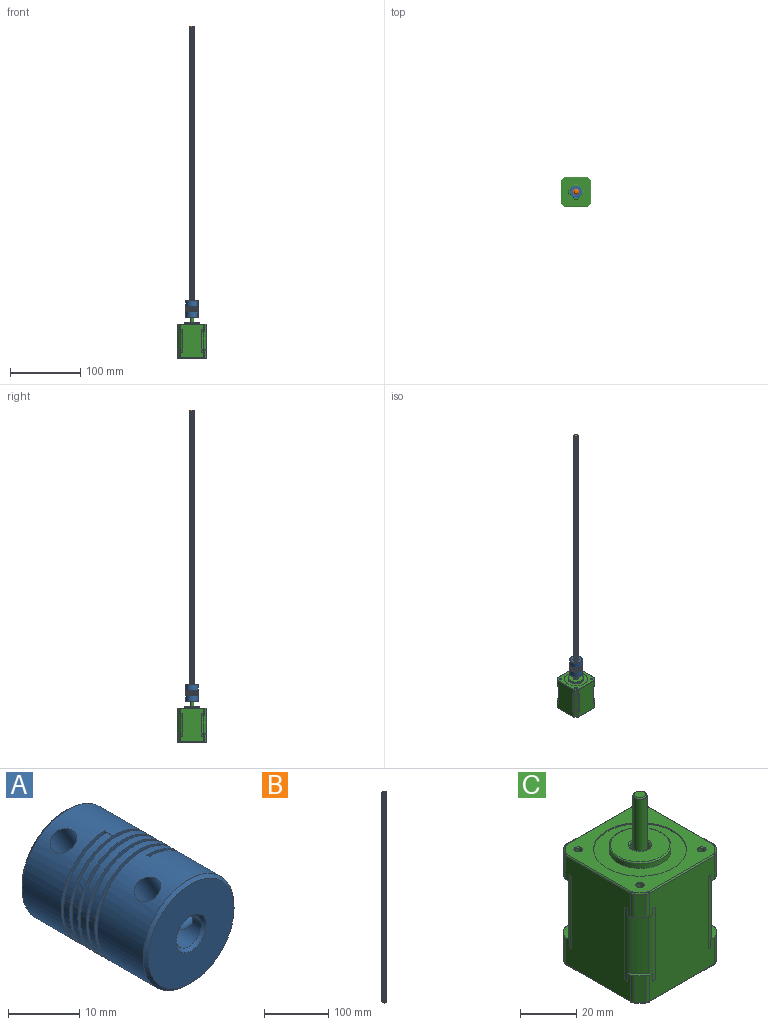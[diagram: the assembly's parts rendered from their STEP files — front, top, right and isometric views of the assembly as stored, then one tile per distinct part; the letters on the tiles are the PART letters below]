
ASSEMBLY  parts=3 mates=2
PART A: 27 faces, bbox 18.3x25x18.3 mm
  f0: cone r=2.75mm half-angle=45deg, axis (0,-1,0), area 12.2mm2, adj f1,f9
  f1: plane 17.31x17mm, normal (0,-1,0), area 198.7mm2, adj f0,f12
  f2: cylinder r=4mm len=4mm, axis (0,-1,0), area 1.3mm2, adj f5,f6,f18
  f3: cylinder r=4mm len=9.42mm, axis (0,-1,0), area 185mm2, adj f4,f10,f14,f16,f17,f18,f19
  f4: cylinder r=4mm len=8mm, axis (0,-1,0), area 29.3mm2, adj f3,f5,f18,f19
  f5: cylinder r=4mm len=8mm, axis (0,-1,0), area 25.1mm2, adj f2,f4,f6,f18,f19
  f6: plane 8.06x7.8mm, normal (0,1,0), area 21.4mm2, adj f2,f5,f7,f18,f19
  f7: cylinder r=2.5mm len=5mm, axis (0,1,0), area 8.3mm2, adj f6,f8,f18,f19
  f8: cylinder r=2.5mm len=5mm, axis (0,1,0), area 18.3mm2, adj f7,f9,f18,f19
  f9: cylinder r=2.5mm len=10.16mm, axis (0,1,0), area 118.5mm2, adj f0,f8,f11,f13,f15,f18,f19
  f10: cone r=4.25mm half-angle=45deg, axis (0,1,0), area 18.9mm2, adj f3,f20
  f11: plane 6.5x0.5mm, normal (1,0,0), area 3.3mm2, adj f9,f18,f19,f25
  f12: cone r=8.75mm half-angle=45deg, axis (0,1,0), area 38.9mm2, adj f1,f25
  f13: cylinder r=2mm len=8.5mm, axis (-0.5,0,0.87), area 86.6mm2, adj f9,f25
  f14: cylinder r=2mm len=6.79mm, axis (-0.5,0,0.87), area 64.8mm2, adj f3,f24
  f15: cylinder r=2mm len=7.5mm, axis (1,0,0), area 86.6mm2, adj f9,f25
  f16: cylinder r=2mm len=5.54mm, axis (1,0,0), area 64.8mm2, adj f3,f24
  f17: plane 5x0.5mm, normal (-1,0,0), area 2.5mm2, adj f3,f18,f19,f24
  f18: bspline ~18.28x18.27mm, area 1098.7mm2, adj f2,f3,f4,f5,f6,f7,f8,f9
  f19: bspline ~18.28x18.27mm, area 1089.5mm2, adj f3,f4,f5,f6,f7,f8,f9,f11
  f20: plane 17.31x17mm, normal (0,1,0), area 163.4mm2, adj f10,f26
  f21: cylinder r=9mm len=18mm, axis (0,1,0), area 66mm2, adj f18,f19,f22,f25
  f22: cylinder r=9mm len=18mm, axis (0,1,0), area 66mm2, adj f18,f19,f21,f23
  f23: cylinder r=9mm len=18mm, axis (0,1,0), area 66mm2, adj f18,f19,f22,f24
  f24: cylinder r=9mm len=18mm, axis (0,1,0), area 452.3mm2, adj f14,f16,f17,f18,f19,f23,f26
  f25: cylinder r=9mm len=18mm, axis (0,1,0), area 518.3mm2, adj f11,f12,f13,f15,f18,f19,f21
  f26: cone r=8.75mm half-angle=45deg, axis (0,-1,0), area 38.9mm2, adj f20,f24
PART B: 31 faces, bbox 8.3x8.3x400 mm
  f0: plane 4x4mm, normal (0,0,1), area 12.6mm2, adj f1
  f1: cone r=4.91mm half-angle=45deg, axis (0,0,-1), area 37.4mm2, adj f0,f2,f15,f16,f17,f18,f19,f20
  f2: bspline ~5.66x2.55mm, area 1.6mm2, adj f1,f3,f30
  f3: bspline ~398.55x8mm, area 1307.8mm2, adj f2,f4,f15,f30
  f4: cone r=0mm half-angle=45deg, axis (0,0,1), area 37.4mm2, adj f3,f5,f6,f7,f8,f9,f10,f11
  f5: bspline ~398.55x8.26mm, area 1307.8mm2, adj f4,f6,f21,f22
  f6: bspline ~398.45x8.26mm, area 554.1mm2, adj f4,f5,f7,f19,f20
  f7: bspline ~398.55x8.26mm, area 1307.2mm2, adj f4,f6,f17,f18
  f8: bspline ~398.55x8mm, area 1307.2mm2, adj f4,f15,f16,f17
  f9: plane 4x4mm, normal (0,0,-1), area 12.6mm2, adj f4
  f10: bspline ~398.55x8mm, area 1307.8mm2, adj f4,f28,f29,f30
  f11: bspline ~398.55x8mm, area 1307.2mm2, adj f4,f26,f27,f28
  f12: bspline ~398.55x8.26mm, area 1307.7mm2, adj f4,f13,f25,f26
  f13: bspline ~398.45x8.26mm, area 554.1mm2, adj f4,f12,f14,f24
  f14: bspline ~398.55x8.26mm, area 1307mm2, adj f4,f13,f22,f23
  f15: bspline ~398.45x8mm, area 554.1mm2, adj f1,f3,f4,f8
  f16: bspline ~4x4mm, area 1.6mm2, adj f1,f8,f17
  f17: cylinder r=3mm len=398mm, axis (0,0,-1), area 373.9mm2, adj f1,f4,f7,f8,f16,f18
  f18: bspline ~5.64x2.55mm, area 1.6mm2, adj f1,f7,f17
  f19: bspline ~4.33x3.78mm, area 0mm2, adj f1,f6
  f20: bspline ~2.72x1.45mm, area 0mm2, adj f1,f6
  f21: bspline ~4.33x3.87mm, area 1.6mm2, adj f1,f5,f22
  f22: cylinder r=3mm len=398mm, axis (0,0,-1), area 477.8mm2, adj f1,f4,f5,f14,f21,f23
  f23: bspline ~5.64x2.55mm, area 1.6mm2, adj f1,f14,f22,f24
  f24: bspline ~4.33x3.78mm, area 0mm2, adj f1,f13,f23,f25
  f25: bspline ~4.33x3.87mm, area 1.6mm2, adj f1,f12,f24,f26
  f26: cylinder r=3mm len=398mm, axis (0,0,-1), area 583.4mm2, adj f1,f4,f11,f12,f25,f27
  f27: bspline ~5.66x2.55mm, area 1.6mm2, adj f1,f11,f26
  f28: bspline ~398.45x8mm, area 554.1mm2, adj f1,f4,f10,f11
  f29: bspline ~4x4mm, area 1.6mm2, adj f1,f10,f30
  f30: cylinder r=3mm len=398mm, axis (0,0,-1), area 478.3mm2, adj f1,f2,f3,f4,f10,f29
PART C: 162 faces, bbox 42.3x42.3x72 mm
  f0: cylinder r=1.25mm len=41.7mm, axis (0,0,-1), area 327.5mm2, adj f143,f160
  f1: cylinder r=1.25mm len=41.7mm, axis (0,0,-1), area 327.5mm2, adj f142,f158
  f2: cylinder r=1.25mm len=41.7mm, axis (0,0,-1), area 327.5mm2, adj f141,f156
  f3: cylinder r=1.25mm len=41.7mm, axis (0,0,-1), area 327.5mm2, adj f144,f154
  f4: cylinder r=8mm len=16mm, axis (0,0,1), area 125.7mm2, adj f13,f152
  f5: plane 2.47x0.85mm, normal (0,0,1), area 0.2mm2, adj f15,f24,f75
  f6: plane 2.47x0.85mm, normal (0,0,1), area 0.2mm2, adj f14,f23,f76
  f7: plane 2.47x0.85mm, normal (0,0,1), area 0.2mm2, adj f17,f23,f77
  f8: plane 2.47x0.85mm, normal (0,0,1), area 0.2mm2, adj f16,f26,f78
  f9: plane 2.47x0.85mm, normal (0,0,1), area 0.2mm2, adj f19,f26,f79
  f10: plane 2.47x0.85mm, normal (0,0,1), area 0.2mm2, adj f18,f25,f80
  f11: plane 2.47x0.85mm, normal (0,0,1), area 0.2mm2, adj f21,f25,f81
  f12: plane 2.47x0.85mm, normal (0,0,1), area 0.2mm2, adj f20,f24,f82
  f13: plane 31x31mm, normal (0,0,1), area 553.7mm2, adj f4,f74
  f14: cylinder r=25.6mm len=3.5mm, axis (0,0,-1), area 5mm2, adj f6,f23,f33,f76
  f15: cylinder r=25.6mm len=3.5mm, axis (0,0,-1), area 5mm2, adj f5,f24,f33,f75
  f16: cylinder r=25.6mm len=3.5mm, axis (0,0,-1), area 5mm2, adj f8,f26,f35,f78
  f17: cylinder r=25.6mm len=3.5mm, axis (0,0,-1), area 5mm2, adj f7,f23,f35,f77
  f18: cylinder r=25.6mm len=3.5mm, axis (0,0,-1), area 5mm2, adj f10,f25,f37,f80
  f19: cylinder r=25.6mm len=3.5mm, axis (0,0,-1), area 5mm2, adj f9,f26,f37,f79
  f20: cylinder r=25.6mm len=3.5mm, axis (0,0,-1), area 5mm2, adj f12,f24,f39,f82
  f21: cylinder r=25.6mm len=3.5mm, axis (0,0,-1), area 5mm2, adj f11,f25,f39,f81
  f22: cylinder r=4.5mm len=9mm, axis (0,0,-1), area 70.7mm2, adj f31,f45
  f23: plane 47x32.74mm, normal (1,0,0), area 1368.1mm2, adj f6,f7,f14,f17,f33,f35,f47,f48
  f24: plane 47x32.74mm, normal (0,1,0), area 1368.1mm2, adj f5,f12,f15,f20,f33,f39,f46,f53
  f25: plane 47x32.74mm, normal (-1,0,0), area 1368.1mm2, adj f10,f11,f18,f21,f37,f39,f51,f52
  f26: plane 47x32.74mm, normal (0,-1,0), area 1368.1mm2, adj f8,f9,f16,f19,f35,f37,f49,f50
  f27: cylinder r=1.25mm len=2.5mm, axis (0,0,-1), area 11.8mm2, adj f43,f161
  f28: cylinder r=1.25mm len=2.5mm, axis (0,0,-1), area 11.8mm2, adj f42,f159
  f29: cylinder r=1.25mm len=2.5mm, axis (0,0,-1), area 11.8mm2, adj f41,f157
  f30: cylinder r=1.25mm len=2.5mm, axis (0,0,-1), area 11.8mm2, adj f40,f155
  f31: plane 41x41mm, normal (0,0,-1), area 1415.7mm2, adj f22,f40,f41,f42,f43,f54,f55,f56
  f32: plane 11.5x2.63mm, normal (0.71,0.71,0), area 42.7mm2, adj f33,f46,f47,f63
  f33: plane 6.36x6.36mm, normal (0,0,1), area 10.4mm2, adj f14,f15,f23,f24,f32,f46,f47,f70
  f34: plane 11.5x2.63mm, normal (0.71,-0.71,0), area 42.7mm2, adj f35,f48,f49,f68
  f35: plane 6.36x6.36mm, normal (0,0,1), area 10.4mm2, adj f16,f17,f23,f26,f34,f48,f49,f71
  f36: plane 11.5x2.63mm, normal (-0.71,-0.71,0), area 42.7mm2, adj f37,f50,f51,f60
  f37: plane 6.36x6.36mm, normal (0,0,1), area 10.4mm2, adj f18,f19,f25,f26,f36,f50,f51,f72
  f38: plane 11.5x2.63mm, normal (-0.71,0.71,0), area 42.7mm2, adj f39,f52,f53,f55
  f39: plane 6.36x6.36mm, normal (0,0,1), area 10.4mm2, adj f20,f21,f24,f25,f38,f52,f53,f73
  f40: cone r=3.75mm half-angle=45deg, axis (0,0,-1), area 55.5mm2, adj f30,f31
  f41: cone r=3.75mm half-angle=45deg, axis (0,0,-1), area 55.5mm2, adj f29,f31
  f42: cone r=3.75mm half-angle=45deg, axis (0,0,-1), area 55.5mm2, adj f28,f31
  f43: cone r=3.75mm half-angle=45deg, axis (0,0,-1), area 55.5mm2, adj f27,f31
  f44: cylinder r=8mm len=16mm, axis (0,0,1), area 75.4mm2, adj f45,f153
  f45: plane 16x16mm, normal (0,0,1), area 137.4mm2, adj f22,f44
  f46: cylinder r=2mm len=11.5mm, axis (0,0,-1), area 18.1mm2, adj f24,f32,f33,f61
  f47: cylinder r=2mm len=11.5mm, axis (0,0,-1), area 18.1mm2, adj f23,f32,f33,f65
  f48: cylinder r=2mm len=11.5mm, axis (0,0,-1), area 18.1mm2, adj f23,f34,f35,f69
  f49: cylinder r=2mm len=11.5mm, axis (0,0,1), area 18.1mm2, adj f26,f34,f35,f66
  f50: cylinder r=2mm len=11.5mm, axis (0,0,-1), area 18.1mm2, adj f26,f36,f37,f62
  f51: cylinder r=2mm len=11.5mm, axis (0,0,-1), area 18.1mm2, adj f25,f36,f37,f58
  f52: cylinder r=2mm len=11.5mm, axis (0,0,-1), area 18.1mm2, adj f25,f38,f39,f54
  f53: cylinder r=2mm len=11.5mm, axis (0,0,1), area 18.1mm2, adj f24,f38,f39,f57
  f54: torus R=1.5mm, axis (0,0,1), area 1.1mm2, adj f31,f52,f55,f56
  f55: cylinder r=0.5mm len=2.98mm, axis (-0.71,-0.71,0), area 2.9mm2, adj f31,f38,f54,f57
  f56: cylinder r=0.5mm len=32.74mm, axis (0,-1,0), area 25.7mm2, adj f25,f31,f54,f58
  f57: torus R=1.5mm, axis (0,0,1), area 1.1mm2, adj f31,f53,f55,f59
  f58: torus R=1.5mm, axis (0,0,1), area 1.1mm2, adj f31,f51,f56,f60
  f59: cylinder r=0.5mm len=32.74mm, axis (-1,0,0), area 25.7mm2, adj f24,f31,f57,f61
  f60: cylinder r=0.5mm len=2.98mm, axis (0.71,-0.71,0), area 2.9mm2, adj f31,f36,f58,f62
  f61: torus R=1.5mm, axis (0,0,1), area 1.1mm2, adj f31,f46,f59,f63
  f62: torus R=1.5mm, axis (0,0,1), area 1.1mm2, adj f31,f50,f60,f64
  f63: cylinder r=0.5mm len=2.98mm, axis (-0.71,0.71,0), area 2.9mm2, adj f31,f32,f61,f65
  f64: cylinder r=0.5mm len=32.74mm, axis (1,0,0), area 25.7mm2, adj f26,f31,f62,f66
  f65: torus R=1.5mm, axis (0,0,1), area 1.1mm2, adj f31,f47,f63,f67
  f66: torus R=1.5mm, axis (0,0,1), area 1.1mm2, adj f31,f49,f64,f68
  f67: cylinder r=0.5mm len=32.74mm, axis (0,1,0), area 25.7mm2, adj f23,f31,f65,f69
  f68: cylinder r=0.5mm len=2.98mm, axis (0.71,0.71,0), area 2.9mm2, adj f31,f34,f66,f69
  f69: torus R=1.5mm, axis (0,0,1), area 1.1mm2, adj f31,f48,f67,f68
  f70: cylinder r=25.6mm len=25.4mm, axis (0,0,-1), area 156.8mm2, adj f33,f75,f76,f112
  f71: cylinder r=25.6mm len=25.4mm, axis (0,0,-1), area 156.8mm2, adj f35,f77,f78,f113
  f72: cylinder r=25.6mm len=25.4mm, axis (0,0,-1), area 156.8mm2, adj f37,f79,f80,f111
  f73: cylinder r=25.6mm len=25.4mm, axis (0,0,-1), area 156.8mm2, adj f39,f81,f82,f110
  f74: cylinder r=15.5mm len=31.5mm, axis (0,0,-1), area 3067.8mm2, adj f13,f100
  f75: cylinder r=4mm len=31.5mm, axis (0,0,-1), area 83.8mm2, adj f5,f15,f24,f70,f88,f91
  f76: cylinder r=4mm len=31.5mm, axis (0,0,-1), area 83.8mm2, adj f6,f14,f23,f70,f87,f98
  f77: cylinder r=4mm len=31.5mm, axis (0,0,-1), area 83.8mm2, adj f7,f17,f23,f71,f90,f97
  f78: cylinder r=4mm len=31.5mm, axis (0,0,-1), area 83.8mm2, adj f8,f16,f26,f71,f89,f96
  f79: cylinder r=4mm len=31.5mm, axis (0,0,-1), area 83.8mm2, adj f9,f19,f26,f72,f86,f95
  f80: cylinder r=4mm len=31.5mm, axis (0,0,-1), area 83.8mm2, adj f10,f18,f25,f72,f85,f94
  f81: cylinder r=4mm len=31.5mm, axis (0,0,-1), area 83.8mm2, adj f11,f21,f25,f73,f84,f93
  f82: cylinder r=4mm len=31.5mm, axis (0,0,-1), area 83.8mm2, adj f12,f20,f24,f73,f83,f92
  f83: cylinder r=25.6mm len=2.6mm, axis (0,0,1), area 3.7mm2, adj f24,f82,f92,f110
  f84: cylinder r=25.6mm len=2.6mm, axis (0,0,1), area 3.7mm2, adj f25,f81,f93,f110
  f85: cylinder r=25.6mm len=2.6mm, axis (0,0,1), area 3.7mm2, adj f25,f80,f94,f111
  f86: cylinder r=25.6mm len=2.6mm, axis (0,0,1), area 3.7mm2, adj f26,f79,f95,f111
  f87: cylinder r=25.6mm len=2.6mm, axis (0,0,1), area 3.7mm2, adj f23,f76,f98,f112
  f88: cylinder r=25.6mm len=2.6mm, axis (0,0,1), area 3.7mm2, adj f24,f75,f91,f112
  f89: cylinder r=25.6mm len=2.6mm, axis (0,0,1), area 3.7mm2, adj f26,f78,f96,f113
  f90: cylinder r=25.6mm len=2.6mm, axis (0,0,1), area 3.7mm2, adj f23,f77,f97,f113
  f91: plane 2.47x0.85mm, normal (0,0,-1), area 0.2mm2, adj f24,f75,f88
  f92: plane 2.47x0.85mm, normal (0,0,-1), area 0.2mm2, adj f24,f82,f83
  f93: plane 2.47x0.85mm, normal (0,0,-1), area 0.2mm2, adj f25,f81,f84
  f94: plane 2.47x0.85mm, normal (0,0,-1), area 0.2mm2, adj f25,f80,f85
  f95: plane 2.47x0.85mm, normal (0,0,-1), area 0.2mm2, adj f26,f79,f86
  f96: plane 2.47x0.85mm, normal (0,0,-1), area 0.2mm2, adj f26,f78,f89
  f97: plane 2.47x0.85mm, normal (0,0,-1), area 0.2mm2, adj f23,f77,f90
  f98: plane 2.47x0.85mm, normal (0,0,-1), area 0.2mm2, adj f23,f76,f87
  f99: cylinder r=3.65mm len=7.3mm, axis (0,0,-1), area 20.6mm2, adj f115,f140
  f100: plane 31x31mm, normal (0,0,-1), area 553.7mm2, adj f74,f114
  f101: plane 10.1x2.63mm, normal (-0.71,-0.71,0), area 37.5mm2, adj f111,f116,f117,f134
  f102: plane 10.1x2.63mm, normal (0.71,-0.71,0), area 37.5mm2, adj f113,f122,f123,f126
  f103: plane 10.1x2.63mm, normal (0.71,0.71,0), area 37.5mm2, adj f112,f120,f121,f129
  f104: plane 10.1x2.63mm, normal (-0.71,0.71,0), area 37.5mm2, adj f110,f118,f119,f137
  f105: cylinder r=16.5mm len=33mm, axis (0,0,-1), area 51.8mm2, adj f106,f107
  f106: plane 41x41mm, normal (0,0,1), area 770.5mm2, adj f105,f124,f125,f126,f127,f128,f129,f130
  f107: plane 33x33mm, normal (0,0,1), area 475.2mm2, adj f105,f108
  f108: cylinder r=11mm len=22mm, axis (0,0,-1), area 138.2mm2, adj f107,f145
  f109: plane 21x21mm, normal (0,0,1), area 292.3mm2, adj f140,f145
  f110: plane 6.36x6.36mm, normal (0,0,-1), area 10.4mm2, adj f24,f25,f73,f83,f84,f104,f118,f119
  f111: plane 6.36x6.36mm, normal (0,0,-1), area 10.4mm2, adj f25,f26,f72,f85,f86,f101,f116,f117
  f112: plane 6.36x6.36mm, normal (0,0,-1), area 10.4mm2, adj f23,f24,f70,f87,f88,f103,f120,f121
  f113: plane 6.36x6.36mm, normal (0,0,-1), area 10.4mm2, adj f23,f26,f71,f89,f90,f102,f122,f123
  f114: cylinder r=8mm len=16mm, axis (0,0,-1), area 432.3mm2, adj f100,f115
  f115: plane 16x16mm, normal (0,0,-1), area 159.2mm2, adj f99,f114
  f116: cylinder r=2mm len=10.1mm, axis (0,0,-1), area 15.9mm2, adj f26,f101,f111,f132
  f117: cylinder r=2mm len=10.1mm, axis (0,0,-1), area 15.9mm2, adj f25,f101,f111,f136
  f118: cylinder r=2mm len=10.1mm, axis (0,0,-1), area 15.9mm2, adj f25,f104,f110,f139
  f119: cylinder r=2mm len=10.1mm, axis (0,0,1), area 15.9mm2, adj f24,f104,f110,f135
  f120: cylinder r=2mm len=10.1mm, axis (0,0,-1), area 15.9mm2, adj f24,f103,f112,f131
  f121: cylinder r=2mm len=10.1mm, axis (0,0,-1), area 15.9mm2, adj f23,f103,f112,f127
  f122: cylinder r=2mm len=10.1mm, axis (0,0,-1), area 15.9mm2, adj f23,f102,f113,f124
  f123: cylinder r=2mm len=10.1mm, axis (0,0,1), area 15.9mm2, adj f26,f102,f113,f128
  f124: torus R=1.5mm, axis (0,0,1), area 1.1mm2, adj f106,f122,f125,f126
  f125: cylinder r=0.5mm len=32.74mm, axis (0,-1,0), area 25.7mm2, adj f23,f106,f124,f127
  f126: cylinder r=0.5mm len=2.98mm, axis (-0.71,-0.71,0), area 2.9mm2, adj f102,f106,f124,f128
  f127: torus R=1.5mm, axis (0,0,1), area 1.1mm2, adj f106,f121,f125,f129
  f128: torus R=1.5mm, axis (0,0,1), area 1.1mm2, adj f106,f123,f126,f130
  f129: cylinder r=0.5mm len=2.98mm, axis (0.71,-0.71,0), area 2.9mm2, adj f103,f106,f127,f131
  f130: cylinder r=0.5mm len=32.74mm, axis (-1,0,0), area 25.7mm2, adj f26,f106,f128,f132
  f131: torus R=1.5mm, axis (0,0,1), area 1.1mm2, adj f106,f120,f129,f133
  f132: torus R=1.5mm, axis (0,0,1), area 1.1mm2, adj f106,f116,f130,f134
  f133: cylinder r=0.5mm len=32.74mm, axis (1,0,0), area 25.7mm2, adj f24,f106,f131,f135
  f134: cylinder r=0.5mm len=2.98mm, axis (-0.71,0.71,0), area 2.9mm2, adj f101,f106,f132,f136
  f135: torus R=1.5mm, axis (0,0,1), area 1.1mm2, adj f106,f119,f133,f137
  f136: torus R=1.5mm, axis (0,0,1), area 1.1mm2, adj f106,f117,f134,f138
  f137: cylinder r=0.5mm len=2.98mm, axis (0.71,0.71,0), area 2.9mm2, adj f104,f106,f135,f139
  f138: cylinder r=0.5mm len=32.74mm, axis (0,1,0), area 25.7mm2, adj f25,f106,f136,f139
  f139: torus R=1.5mm, axis (0,0,1), area 1.1mm2, adj f106,f118,f137,f138
  f140: torus R=4.15mm, axis (0,0,1), area 18.9mm2, adj f99,f109
  f141: cone r=1.25mm half-angle=45deg, axis (0,0,1), area 3.7mm2, adj f2,f106
  f142: cone r=1.25mm half-angle=45deg, axis (0,0,1), area 3.7mm2, adj f1,f106
  f143: cone r=1.25mm half-angle=45deg, axis (0,0,1), area 3.7mm2, adj f0,f106
  f144: cone r=1.25mm half-angle=45deg, axis (0,0,1), area 3.7mm2, adj f3,f106
  f145: torus R=10.5mm, axis (0,0,1), area 53.4mm2, adj f108,f109
  f146: cone r=2.5mm half-angle=45deg, axis (0,0,1), area 10mm2, adj f151,f152
  f147: cone r=2mm half-angle=45deg, axis (0,0,-1), area 8.6mm2, adj f149,f150,f151
  f148: plane 2.98x0.71mm, normal (0,0,1), area 1mm2, adj f149,f151
  f149: plane 15x2.98mm, normal (0.99,-0.13,0), area 44.5mm2, adj f147,f148,f151
  f150: plane 4x4mm, normal (0,0,1), area 12.6mm2, adj f147
  f151: cylinder r=2.5mm len=65mm, axis (0,0,-1), area 974.4mm2, adj f146,f147,f148,f149
  f152: plane 16x16mm, normal (0,0,1), area 188.5mm2, adj f4,f146
  f153: plane 16x16mm, normal (0,0,-1), area 201.1mm2, adj f44
  f154: plane 2.5x2.5mm, normal (0,0,1), area 4.9mm2, adj f3
  f155: plane 2.5x2.5mm, normal (0,0,-1), area 4.9mm2, adj f30
  f156: plane 2.5x2.5mm, normal (0,0,1), area 4.9mm2, adj f2
  f157: plane 2.5x2.5mm, normal (0,0,-1), area 4.9mm2, adj f29
  f158: plane 2.5x2.5mm, normal (0,0,1), area 4.9mm2, adj f1
  f159: plane 2.5x2.5mm, normal (0,0,-1), area 4.9mm2, adj f28
  f160: plane 2.5x2.5mm, normal (0,0,1), area 4.9mm2, adj f0
  f161: plane 2.5x2.5mm, normal (0,0,-1), area 4.9mm2, adj f27
PLACE A rot(axis=(0.58,0.58,0.58),120deg) t=(55.93,45.39,12.33)mm
PLACE B rot(axis=(-0.01,0,1),0deg) t=(55.93,45.39,27.35)mm
PLACE C t=(55.93,45.39,-44.65)mm fixed
MATE fastened B.f4 <-> C.f105  axis (0,0,-1) through (55.93,45.39,27.35)mm
MATE fastened B.f4 <-> A.f0  axis (0,0,-1) through (55.93,45.39,27.35)mm
